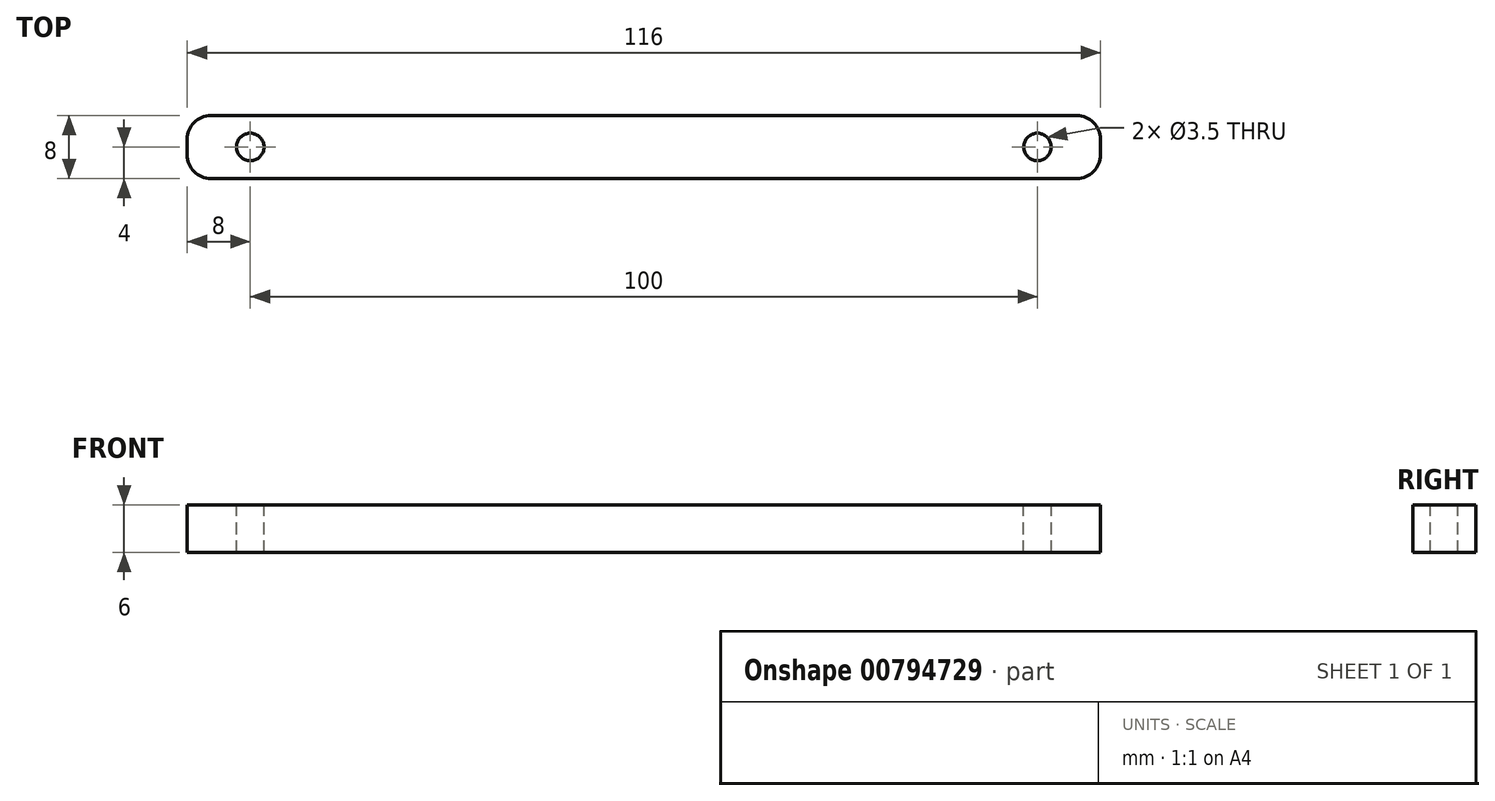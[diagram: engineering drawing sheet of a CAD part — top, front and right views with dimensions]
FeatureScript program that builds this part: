
annotation { "Feature Type Name" : "Feature", "Feature Type Description" : "" }
export const myFeature = defineFeature(function(context is Context, id is Id, definition is map)
    precondition{}
    {
        {
            var Q0;
            Q0=qCreatedBy(makeId("Top.planeOp"),FACE);
            var sketch = newSketch(context, id + "F0", { "sketchPlane" : qUnion([Q0])});
            skLineSegment(sketch, "E0.bottom", {"start": v(-58, 4) * mm, "end": v(58, 4) * mm});
            skLineSegment(sketch, "E0.top", {"start": v(-58, -4) * mm, "end": v(58, -4) * mm});
            skLineSegment(sketch, "E0.left", {"start": v(-58, 4) * mm, "end": v(-58, -4) * mm});
            skLineSegment(sketch, "E0.right", {"start": v(58, 4) * mm, "end": v(58, -4) * mm});
            skSolve(sketch);
        }
        {
            var Q0;
            Q0=makeQuery(id+"F0.imprint","IMPRINT",FACE,{"disambiguationData":[TD([[makeQuery(id+"F0.imprint","IMPRINT",EDGE,{"derivedFrom":sQuery(id+"F0.wireOp",EDGE,"E0.bottom")}),-1.0]])]});
            extrude(context, id + "F1", {"entities" : qUnion([Q0]), "depth" : 6 * mm, "offsetDistance" : 25 * mm});
        }
        {
            var Q0;
            Q0=makeQuery(id+"F1.opExtrude","CAP_FACE",FACE,{"disambiguationData":[OSD([sQuery(id+"F0.wireOp",EDGE,"E0.bottom"),sQuery(id+"F0.wireOp",EDGE,"E0.top"),sQuery(id+"F0.wireOp",EDGE,"E0.left"),sQuery(id+"F0.wireOp",EDGE,"E0.right")])],"isStart":false});
            var sketch = newSketch(context, id + "F2", { "sketchPlane" : qUnion([Q0])});
            skLineSegment(sketch, "E1", {"start": v(-58, 0) * mm, "end": v(58, 0) * mm, "construction": true});
            skPoint(sketch, "E2", {"position": v(-50, 0) * mm});
            skPoint(sketch, "E3", {"position": v(50, 0) * mm});
            skSolve(sketch);
        }
        {
            var Q0;
            Q0=sQuery(id+"F2.wireOp",VERTEX,"E2");
            var Q1;
            Q1=sQuery(id+"F2.wireOp",VERTEX,"E3");
            var Q2;
            Q2=makeQuery(id+"F1.opExtrude","SWEPT_BODY",BODY,{"disambiguationData":[OSD([sQuery(id+"F0.wireOp",EDGE,"E0.bottom"),sQuery(id+"F0.wireOp",EDGE,"E0.top"),sQuery(id+"F0.wireOp",EDGE,"E0.left"),sQuery(id+"F0.wireOp",EDGE,"E0.right")])]});
            hole(context, id + "F3", {"style" : HoleStyle.SIMPLE, "endStyle" : HoleEndStyle.THROUGH, "holeDiameter" : 3.5 * mm, "majorDiameter" : 5 * mm, "isTappedThrough" : true, "tappedDepth" : 12 * mm, "tapClearance" : 3, "locations" : qUnion([Q0, Q1]), "scope" : qUnion([Q2])});
        }
        {
            var Q0;
            Q0=makeQuery(id+"F1.opExtrude","SWEPT_EDGE",EDGE,{"disambiguationData":[OSD([sQuery(id+"F0.wireOp",EDGE,"E0.top"),sQuery(id+"F0.wireOp",EDGE,"E0.left")])]});
            var Q1;
            Q1=makeQuery(id+"F1.opExtrude","SWEPT_EDGE",EDGE,{"disambiguationData":[OSD([sQuery(id+"F0.wireOp",EDGE,"E0.bottom"),sQuery(id+"F0.wireOp",EDGE,"E0.left")])]});
            var Q2;
            Q2=makeQuery(id+"F1.opExtrude","SWEPT_EDGE",EDGE,{"disambiguationData":[OSD([sQuery(id+"F0.wireOp",EDGE,"E0.top"),sQuery(id+"F0.wireOp",EDGE,"E0.right")])]});
            var Q3;
            Q3=makeQuery(id+"F1.opExtrude","SWEPT_EDGE",EDGE,{"disambiguationData":[OSD([sQuery(id+"F0.wireOp",EDGE,"E0.bottom"),sQuery(id+"F0.wireOp",EDGE,"E0.right")])]});
            fillet(context, id + "F4", {"entities" : qUnion([Q0, Q1, Q2, Q3]), "radius" : 3 * mm, "tangentPropagation" : true, "allowEdgeOverflow" : false});
        }
    });
